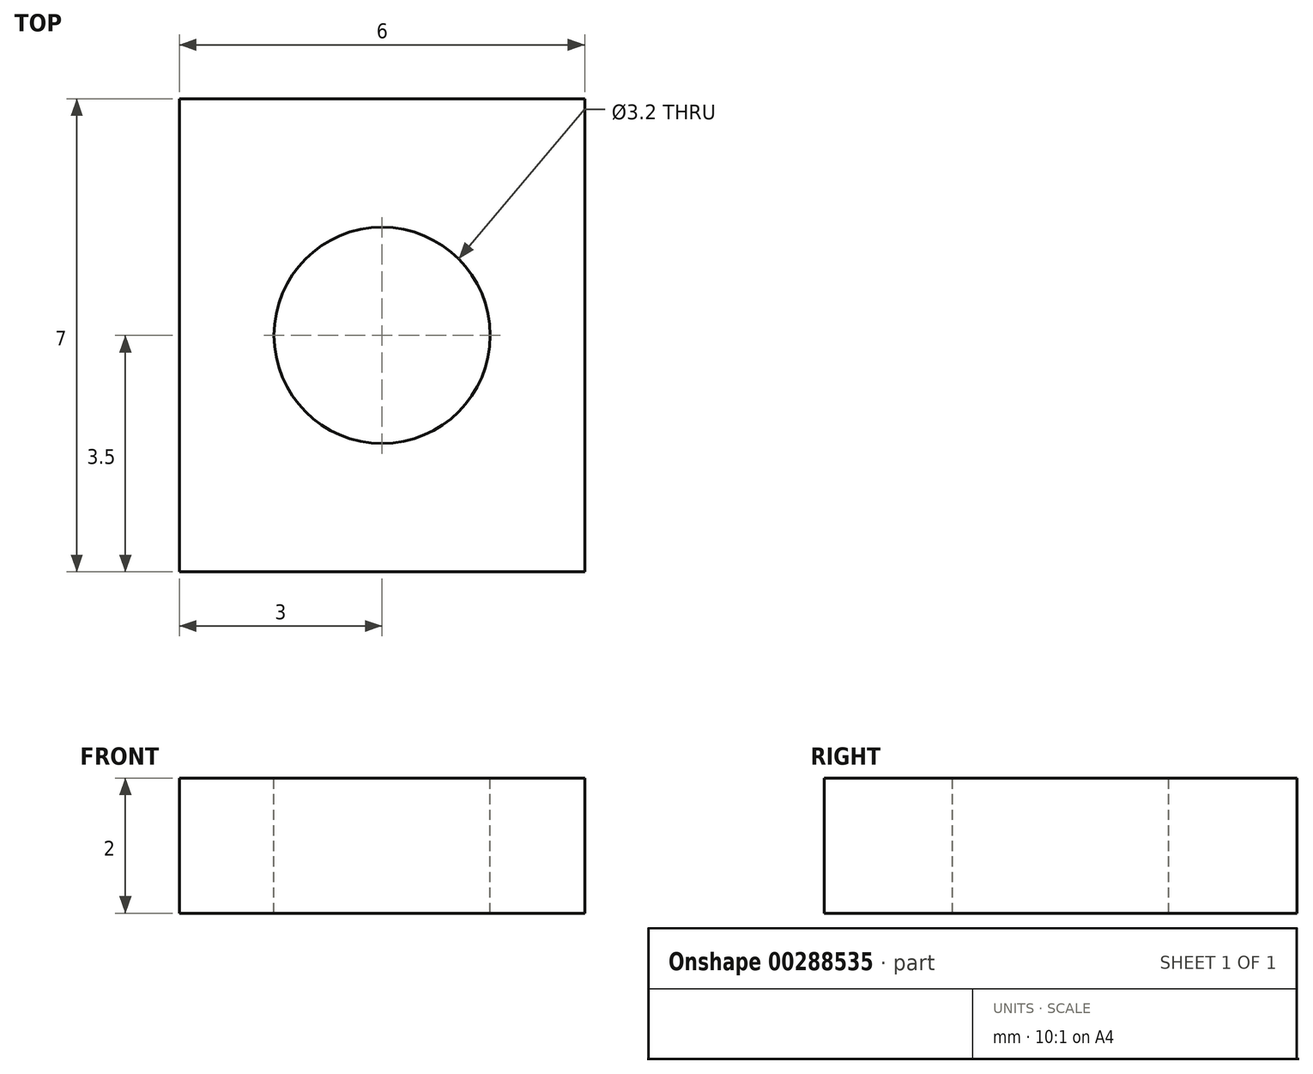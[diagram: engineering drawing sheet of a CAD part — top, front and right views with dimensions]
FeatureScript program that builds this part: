
annotation { "Feature Type Name" : "Feature", "Feature Type Description" : "" }
export const myFeature = defineFeature(function(context is Context, id is Id, definition is map)
    precondition{}
    {
        {
            var Q0;
            Q0=qCreatedBy(makeId("Top.planeOp"),FACE);
            var sketch = newSketch(context, id + "F0", { "sketchPlane" : qUnion([Q0])});
            skLineSegment(sketch, "E0.bottom", {"start": v(3, -3.5) * mm, "end": v(-3, -3.5) * mm});
            skLineSegment(sketch, "E0.top", {"start": v(3, 3.5) * mm, "end": v(-3, 3.5) * mm});
            skLineSegment(sketch, "E0.left", {"start": v(3, -3.5) * mm, "end": v(3, 3.5) * mm});
            skLineSegment(sketch, "E0.right", {"start": v(-3, -3.5) * mm, "end": v(-3, 3.5) * mm});
            skPoint(sketch, "E0.middle", {"position": v(0, 0) * mm});
            skCircle(sketch, "E1", {"center": v(0, 0) * mm, "radius": 1.6 * mm});
            skCircle(sketch, "E2.cCircle", {"center": v(0, 0) * mm, "radius": 2.75 * mm, "construction": true});
            skLineSegment(sketch, "E2.0", {"start": v(2.75, 1.59) * mm, "end": v(2.75, -1.59) * mm});
            skLineSegment(sketch, "E2.1", {"start": v(2.75, -1.59) * mm, "end": v(0, -3.18) * mm, "construction": true});
            skLineSegment(sketch, "E2.2", {"start": v(0, -3.18) * mm, "end": v(-2.75, -1.59) * mm, "construction": true});
            skLineSegment(sketch, "E2.3", {"start": v(-2.75, -1.59) * mm, "end": v(-2.75, 1.59) * mm});
            skLineSegment(sketch, "E2.4", {"start": v(-2.75, 1.59) * mm, "end": v(0, 3.18) * mm, "construction": true});
            skLineSegment(sketch, "E2.5", {"start": v(0, 3.18) * mm, "end": v(2.75, 1.59) * mm, "construction": true});
            skPoint(sketch, "E2.0.midPoint", {"position": v(2.75, 0) * mm});
            skArc(sketch, "E3", {"start": v(2.75, -1.59) * mm, "mid": v(2.67, -1.99) * mm, "end": v(2.43, -2.32) * mm});
            skSolve(sketch);
        }
        {
            var Q0;
            Q0=makeQuery(id+"F0.imprint","IMPRINT",FACE,{"disambiguationData":[TD([[makeQuery(id+"F0.imprint","IMPRINT",EDGE,{"derivedFrom":sQuery(id+"F0.wireOp",EDGE,"E0.bottom")}),-1.0]])]});
            var Q1;
            {var subQ1=sQuery(id+"F0.wireOp",EDGE,"E2.4");var subQ3=sQuery(id+"F0.wireOp",EDGE,"p7mL5oWL-epy6-e4Ch-18hv-DYI8YV9zrZui");var subQ4=makeQuery(id+"F0.imprint","INTERSECT",VERTEX,{"derivedFrom":[subQ1,subQ3]});Q1=makeQuery(id+"F0.imprint","IMPRINT",FACE,{"disambiguationData":[TD([[makeQuery(id+"F0.imprint","IMPRINT",EDGE,{"disambiguationData":[TD([[subQ4,-1.0]])],"derivedFrom":subQ1}),1.0]])]});}
            var Q2;
            {var subQ0=sQuery(id+"F0.wireOp",EDGE,"72b8cb44-5f2a-4b23-8d68-c1266944e514");Q2=makeQuery(id+"F0.imprint","IMPRINT",FACE,{"disambiguationData":[TD([[makeQuery(id+"F0.imprint","IMPRINT",EDGE,{"derivedFrom":subQ0}),-1.0]])]});}
            var Q3;
            {var subQ1=sQuery(id+"F0.wireOp",EDGE,"E2.5");var subQ3=sQuery(id+"F0.wireOp",EDGE,"RkngDp5N-VDl8-j7ax-gwGB-3NiffRGZ0FRz");var subQ4=makeQuery(id+"F0.imprint","INTERSECT",VERTEX,{"derivedFrom":[subQ1,subQ3]});Q3=makeQuery(id+"F0.imprint","IMPRINT",FACE,{"disambiguationData":[TD([[makeQuery(id+"F0.imprint","IMPRINT",EDGE,{"disambiguationData":[TD([[subQ4,1.0]])],"derivedFrom":subQ1}),1.0]])]});}
            var Q4;
            {var subQ0=sQuery(id+"F0.wireOp",EDGE,"52fbc7b4-52a9-4732-8b3b-ba11b8eaf999");Q4=makeQuery(id+"F0.imprint","IMPRINT",FACE,{"disambiguationData":[TD([[makeQuery(id+"F0.imprint","IMPRINT",EDGE,{"derivedFrom":subQ0}),1.0]])]});}
            var Q5;
            Q5=makeQuery(id+"F0.imprint","IMPRINT",FACE,{"disambiguationData":[TD([[makeQuery(id+"F0.imprint","IMPRINT",EDGE,{"derivedFrom":sQuery(id+"F0.wireOp",EDGE,"E1")}),-1.0]])]});
            var Q6;
            {var subQ1=sQuery(id+"F0.wireOp",EDGE,"E2.1");var subQ3=sQuery(id+"F0.wireOp",EDGE,"Uh1s7zSf-JDTe-NH28-jndg-JmfrljfSlsne");var subQ4=makeQuery(id+"F0.imprint","INTERSECT",VERTEX,{"derivedFrom":[subQ1,subQ3]});Q6=makeQuery(id+"F0.imprint","IMPRINT",FACE,{"disambiguationData":[TD([[makeQuery(id+"F0.imprint","IMPRINT",EDGE,{"disambiguationData":[TD([[subQ4,-1.0]])],"derivedFrom":subQ1}),1.0]])]});}
            var Q7;
            {var subQ0=sQuery(id+"F0.wireOp",EDGE,"E3");Q7=makeQuery(id+"F0.imprint","IMPRINT",FACE,{"disambiguationData":[TD([[makeQuery(id+"F0.imprint","IMPRINT",EDGE,{"derivedFrom":subQ0}),-1.0]])]});}
            var Q8;
            {var subQ1=sQuery(id+"F0.wireOp",EDGE,"E2.2");var subQ3=sQuery(id+"F0.wireOp",EDGE,"HT26icJx-fT6e-FU1q-vkdg-eDac6r2f1aKu");var subQ4=makeQuery(id+"F0.imprint","INTERSECT",VERTEX,{"derivedFrom":[subQ1,subQ3]});Q8=makeQuery(id+"F0.imprint","IMPRINT",FACE,{"disambiguationData":[TD([[makeQuery(id+"F0.imprint","IMPRINT",EDGE,{"disambiguationData":[TD([[subQ4,1.0]])],"derivedFrom":subQ1}),1.0]])]});}
            var Q9;
            {var subQ0=sQuery(id+"F0.wireOp",EDGE,"e20f4b52-e160-4fef-9fdc-7976a82d6bc7");Q9=makeQuery(id+"F0.imprint","IMPRINT",FACE,{"disambiguationData":[TD([[makeQuery(id+"F0.imprint","IMPRINT",EDGE,{"derivedFrom":subQ0}),1.0]])]});}
            extrude(context, id + "F1", {"entities" : qUnion([Q0, Q1, Q2, Q3, Q4, Q5, Q6, Q7, Q8, Q9]), "oppositeDirection" : true, "depth" : 4 * mm});
        }
        {
            var Q0;
            Q0=makeQuery(id+"F0.imprint","IMPRINT",FACE,{"disambiguationData":[TD([[makeQuery(id+"F0.imprint","IMPRINT",EDGE,{"derivedFrom":sQuery(id+"F0.wireOp",EDGE,"E1")}),-1.0]])]});
            var Q1;
            Q1=makeQuery(id+"F0.imprint","IMPRINT",FACE,{"disambiguationData":[TD([[makeQuery(id+"F0.imprint","IMPRINT",EDGE,{"derivedFrom":sQuery(id+"F0.wireOp",EDGE,"E2.4")}),1.0]])]});
            var Q2;
            Q2=makeQuery(id+"F0.imprint","IMPRINT",FACE,{"disambiguationData":[TD([[makeQuery(id+"F0.imprint","IMPRINT",EDGE,{"derivedFrom":sQuery(id+"F0.wireOp",EDGE,"E2.1")}),1.0]])]});
            var Q3;
            {var subQ1=sQuery(id+"F0.wireOp",EDGE,"E2.5");var subQ3=sQuery(id+"F0.wireOp",EDGE,"RkngDp5N-VDl8-j7ax-gwGB-3NiffRGZ0FRz");var subQ4=makeQuery(id+"F0.imprint","INTERSECT",VERTEX,{"derivedFrom":[subQ1,subQ3]});Q3=makeQuery(id+"F0.imprint","IMPRINT",FACE,{"disambiguationData":[TD([[makeQuery(id+"F0.imprint","IMPRINT",EDGE,{"disambiguationData":[TD([[subQ4,1.0]])],"derivedFrom":subQ1}),1.0]])]});}
            var Q4;
            {var subQ0=sQuery(id+"F0.wireOp",EDGE,"52fbc7b4-52a9-4732-8b3b-ba11b8eaf999");Q4=makeQuery(id+"F0.imprint","IMPRINT",FACE,{"disambiguationData":[TD([[makeQuery(id+"F0.imprint","IMPRINT",EDGE,{"derivedFrom":subQ0}),1.0]])]});}
            var Q5;
            {var subQ1=sQuery(id+"F0.wireOp",EDGE,"E2.2");var subQ3=sQuery(id+"F0.wireOp",EDGE,"HT26icJx-fT6e-FU1q-vkdg-eDac6r2f1aKu");var subQ4=makeQuery(id+"F0.imprint","INTERSECT",VERTEX,{"derivedFrom":[subQ1,subQ3]});Q5=makeQuery(id+"F0.imprint","IMPRINT",FACE,{"disambiguationData":[TD([[makeQuery(id+"F0.imprint","IMPRINT",EDGE,{"disambiguationData":[TD([[subQ4,1.0]])],"derivedFrom":subQ1}),1.0]])]});}
            var Q6;
            {var subQ0=sQuery(id+"F0.wireOp",EDGE,"e20f4b52-e160-4fef-9fdc-7976a82d6bc7");Q6=makeQuery(id+"F0.imprint","IMPRINT",FACE,{"disambiguationData":[TD([[makeQuery(id+"F0.imprint","IMPRINT",EDGE,{"derivedFrom":subQ0}),1.0]])]});}
            extrude(context, id + "F2", {"entities" : qUnion([Q0, Q1, Q2, Q3, Q4, Q5, Q6]), "operationType" : NewBodyOperationType.REMOVE, "oppositeDirection" : true, "depth" : 2 * mm});
        }
    });
